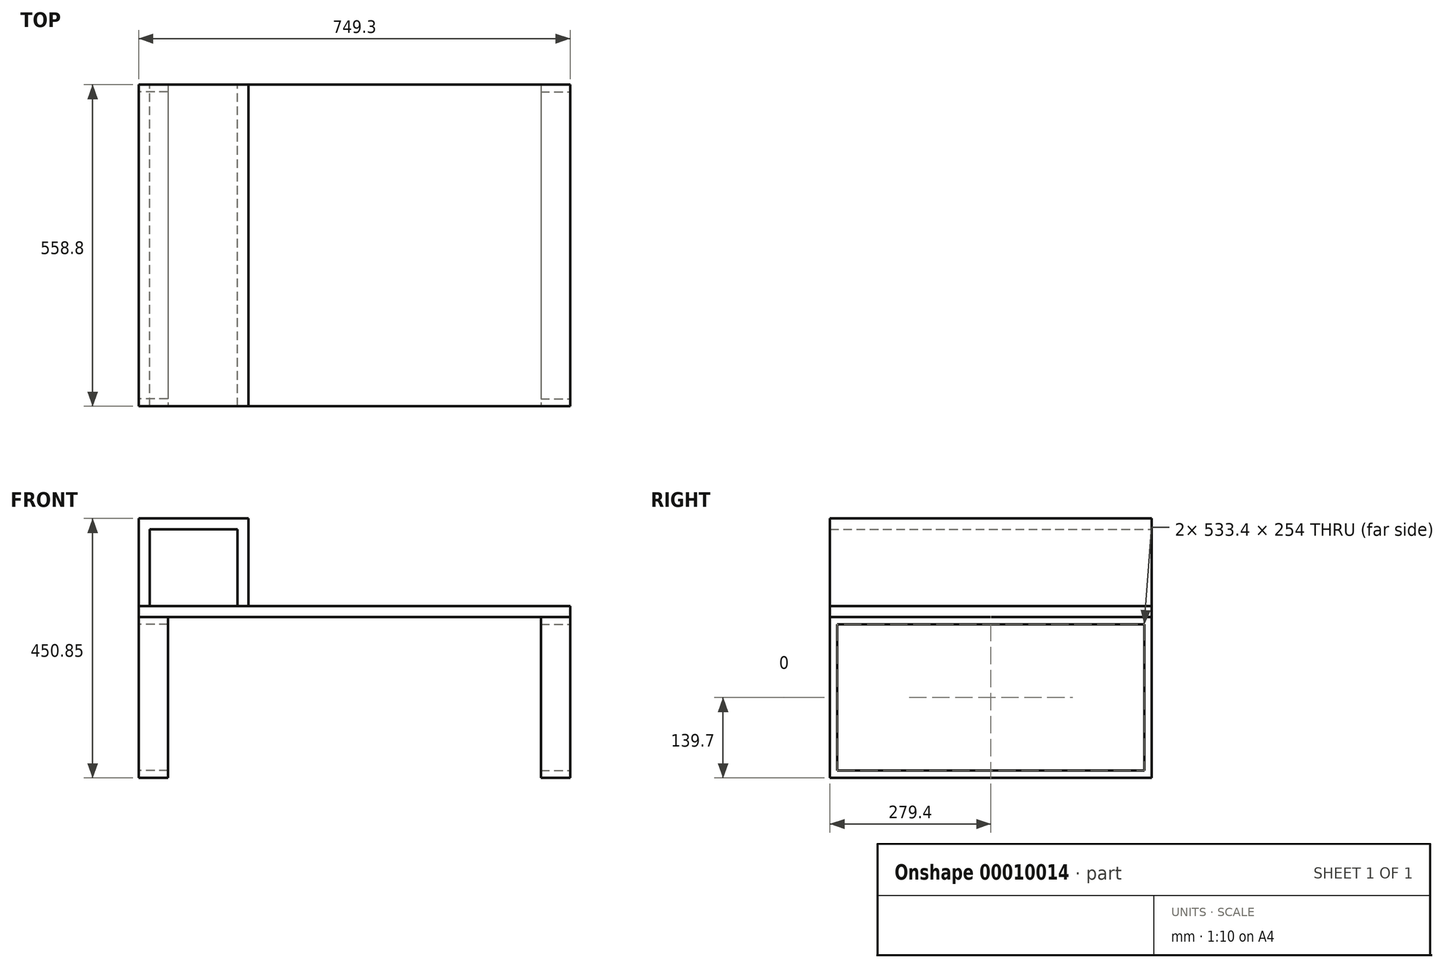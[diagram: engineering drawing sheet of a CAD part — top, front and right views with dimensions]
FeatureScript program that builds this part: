
annotation { "Feature Type Name" : "Feature", "Feature Type Description" : "" }
export const myFeature = defineFeature(function(context is Context, id is Id, definition is map)
    precondition{}
    {
        {
            var Q0;
            Q0=qCreatedBy(makeId("Top.planeOp"),FACE);
            var sketch = newSketch(context, id + "F0", { "sketchPlane" : qUnion([Q0])});
            skLineSegment(sketch, "E0.bottom", {"start": v(374.65, 279.4) * mm, "end": v(-374.65, 279.4) * mm});
            skLineSegment(sketch, "E0.top", {"start": v(374.65, -279.4) * mm, "end": v(-374.65, -279.4) * mm});
            skLineSegment(sketch, "E0.left", {"start": v(374.65, 279.4) * mm, "end": v(374.65, -279.4) * mm});
            skLineSegment(sketch, "E0.right", {"start": v(-374.65, 279.4) * mm, "end": v(-374.65, -279.4) * mm});
            skPoint(sketch, "E0.middle", {"position": v(0, 0) * mm});
            skSolve(sketch);
        }
        {
            var Q0;
            Q0 = qSketchRegion(id + "F0", true);
            extrude(context, id + "F1", {"entities" : qUnion([Q0]), "depth" : 19.05 * mm});
        }
        {
            var Q0;
            Q0=qCreatedBy(makeId("Front.planeOp"),FACE);
            var sketch = newSketch(context, id + "F2", { "sketchPlane" : qUnion([Q0])});
            skLineSegment(sketch, "E1.bottom", {"start": v(-374.65, 19.05) * mm, "end": v(-355.6, 19.05) * mm});
            skLineSegment(sketch, "E1.top", {"start": v(-374.65, 171.45) * mm, "end": v(-184.15, 171.45) * mm});
            skLineSegment(sketch, "E1.left", {"start": v(-374.65, 19.05) * mm, "end": v(-374.65, 171.45) * mm});
            skLineSegment(sketch, "E1.right", {"start": v(-184.15, 19.05) * mm, "end": v(-184.15, 171.45) * mm});
            skLineSegment(sketch, "E2.top", {"start": v(-355.6, 152.4) * mm, "end": v(-203.2, 152.4) * mm});
            skLineSegment(sketch, "E2.left", {"start": v(-355.6, 19.05) * mm, "end": v(-355.6, 152.4) * mm});
            skLineSegment(sketch, "E2.right", {"start": v(-203.2, 19.05) * mm, "end": v(-203.2, 152.4) * mm});
            skLineSegment(sketch, "E3.trimOffspring", {"start": v(-203.2, 19.05) * mm, "end": v(-184.15, 19.05) * mm});
            skSolve(sketch);
        }
        {
            var Q0;
            Q0 = qSketchRegion(id + "F2", true);
            var Q1;
            Q1=makeQuery(id+"F1.opExtrude","SWEPT_FACE",FACE,{"disambiguationData":[OSD([sQuery(id+"F0.wireOp",EDGE,"E0.bottom")])]});
            var Q2;
            Q2=makeQuery(id+"F1.opExtrude","SWEPT_FACE",FACE,{"disambiguationData":[OSD([sQuery(id+"F0.wireOp",EDGE,"E0.bottom")])]});
            extrude(context, id + "F3", {"entities" : qUnion([Q0]), "endBound" : BoundingType.SYMMETRIC, "endBoundEntityFace" : qUnion([Q1]), "depth" : 558.8 * mm});
        }
        {
            var Q0;
            Q0=makeQuery(id+"F1.opExtrude","SWEPT_FACE",FACE,{"disambiguationData":[OSD([sQuery(id+"F0.wireOp",EDGE,"E0.right")])]});
            var sketch = newSketch(context, id + "F4", { "sketchPlane" : qUnion([Q0])});
            skLineSegment(sketch, "E4.bottom", {"start": v(-279.4, 0) * mm, "end": v(279.4, 0) * mm});
            skLineSegment(sketch, "E4.top", {"start": v(-279.4, -279.4) * mm, "end": v(279.4, -279.4) * mm});
            skLineSegment(sketch, "E4.left", {"start": v(-279.4, 0) * mm, "end": v(-279.4, -279.4) * mm});
            skLineSegment(sketch, "E4.right", {"start": v(279.4, 0) * mm, "end": v(279.4, -279.4) * mm});
            skLineSegment(sketch, "E5.0", {"start": v(266.7, -12.7) * mm, "end": v(266.7, -266.7) * mm});
            skLineSegment(sketch, "E5.1", {"start": v(-266.7, -12.7) * mm, "end": v(266.7, -12.7) * mm});
            skLineSegment(sketch, "E5.2", {"start": v(-266.7, -12.7) * mm, "end": v(-266.7, -266.7) * mm});
            skLineSegment(sketch, "E5.3", {"start": v(-266.7, -266.7) * mm, "end": v(266.7, -266.7) * mm});
            skSolve(sketch);
        }
        {
            var Q0;
            Q0=makeQuery(id+"F4.imprint","IMPRINT",FACE,{"disambiguationData":[TD([[makeQuery(id+"F4.imprint","IMPRINT",EDGE,{"derivedFrom":sQuery(id+"F4.wireOp",EDGE,"E4.bottom")}),-1.0]])]});
            extrude(context, id + "F5", {"entities" : qUnion([Q0]), "oppositeDirection" : true, "depth" : 50.8 * mm});
        }
        {
            var Q0;
            Q0=makeQuery(id+"F1.opExtrude","SWEPT_FACE",FACE,{"disambiguationData":[OSD([sQuery(id+"F0.wireOp",EDGE,"E0.left")])]});
            var sketch = newSketch(context, id + "F6", { "sketchPlane" : qUnion([Q0])});
            skLineSegment(sketch, "E6.0.0", {"start": v(-279.4, 0) * mm, "end": v(-279.4, -279.4) * mm});
            skLineSegment(sketch, "E6.0.1", {"start": v(-279.4, -279.4) * mm, "end": v(279.4, -279.4) * mm});
            skLineSegment(sketch, "E6.0.2", {"start": v(279.4, -279.4) * mm, "end": v(279.4, 0) * mm});
            skLineSegment(sketch, "E6.0.3", {"start": v(279.4, 0) * mm, "end": v(-279.4, 0) * mm});
            skLineSegment(sketch, "E7.0", {"start": v(266.7, -266.7) * mm, "end": v(-266.7, -266.7) * mm});
            skLineSegment(sketch, "E8.0", {"start": v(266.7, -12.7) * mm, "end": v(266.7, -266.7) * mm});
            skLineSegment(sketch, "E9.0", {"start": v(266.7, -12.7) * mm, "end": v(-266.7, -12.7) * mm});
            skLineSegment(sketch, "E10.0", {"start": v(-266.7, -12.7) * mm, "end": v(-266.7, -266.7) * mm});
            skSolve(sketch);
        }
        {
            var Q0;
            Q0 = qSketchRegion(id + "F6", true);
            extrude(context, id + "F7", {"entities" : qUnion([Q0]), "oppositeDirection" : true, "depth" : 50.8 * mm});
        }
    });
